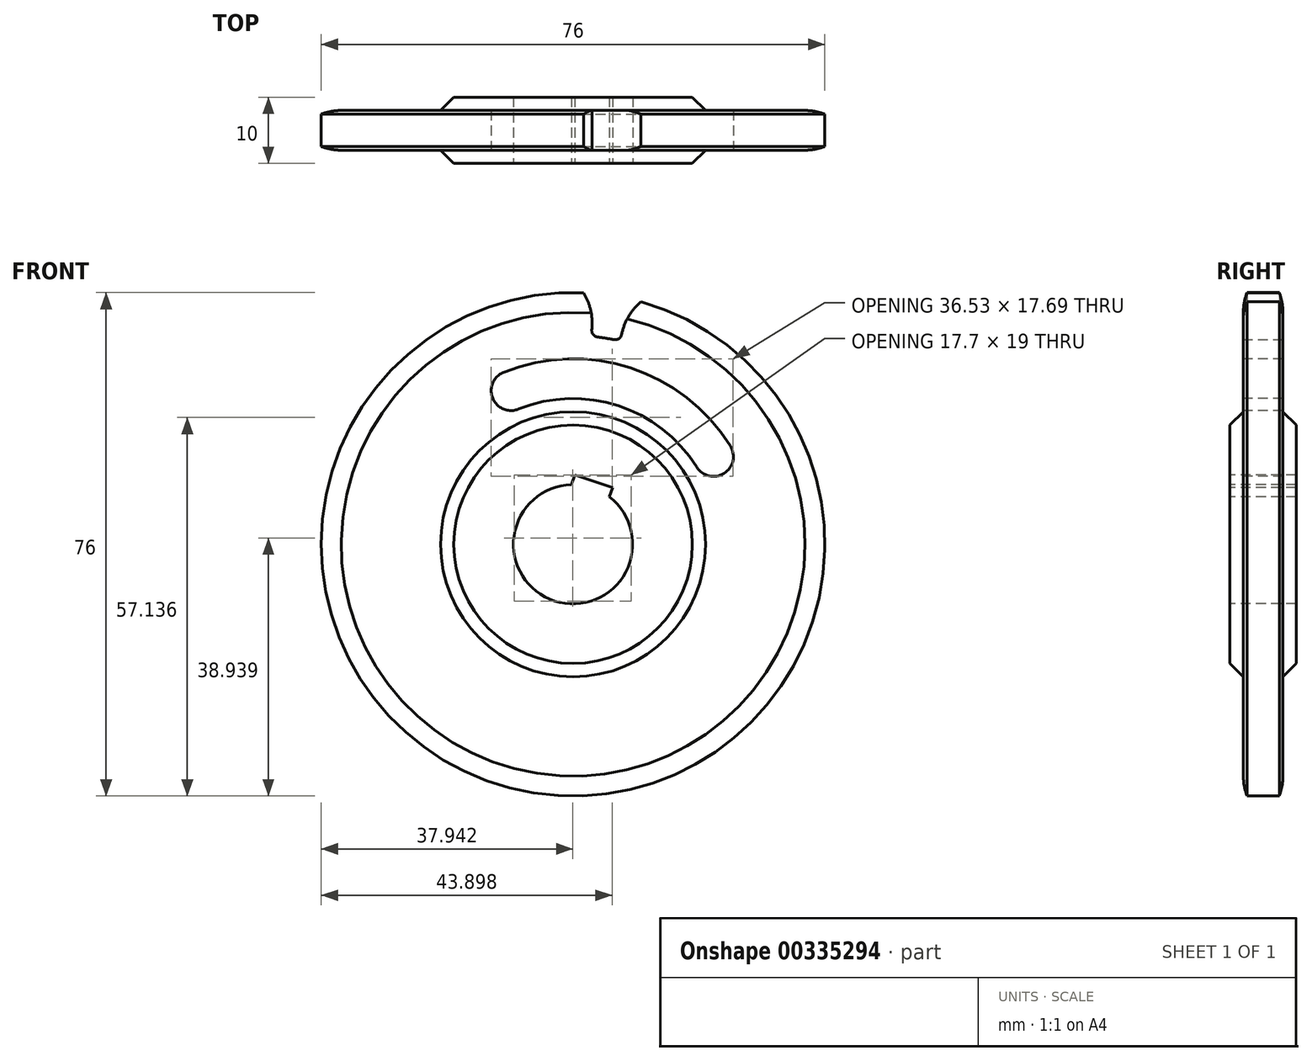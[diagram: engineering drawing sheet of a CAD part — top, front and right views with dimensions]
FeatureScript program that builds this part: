
annotation { "Feature Type Name" : "Feature", "Feature Type Description" : "" }
export const myFeature = defineFeature(function(context is Context, id is Id, definition is map)
    precondition{}
    {
        {
            var Q0;
            Q0=qCreatedBy(makeId("Front.planeOp"),FACE);
            var sketch = newSketch(context, id + "F0", { "sketchPlane" : qUnion([Q0])});
            skCircle(sketch, "E0", {"center": v(0, 0) * mm, "radius": 38 * mm});
            skSolve(sketch);
        }
        {
            var Q0;
            Q0=makeQuery(id+"F0.imprint","IMPRINT",FACE,{"disambiguationData":[TD([[makeQuery(id+"F0.imprint","IMPRINT",EDGE,{"derivedFrom":sQuery(id+"F0.wireOp",EDGE,"E0")}),1.0]])]});
            extrude(context, id + "F1", {"entities" : qUnion([Q0]), "depth" : 6 * mm, "symmetric" : true});
        }
        {
            var Q0;
            Q0=makeQuery(id+"F1.opExtrude","CAP_FACE",FACE,{"disambiguationData":[OSD([sQuery(id+"F0.wireOp",EDGE,"E0")])],"isStart":false});
            var sketch = newSketch(context, id + "F2", { "sketchPlane" : qUnion([Q0])});
            skLineSegment(sketch, "E1", {"start": v(0, 0) * mm, "end": v(0, 38) * mm, "construction": true});
            skArc(sketch, "E2", {"start": v(-1.57, 37.97) * mm, "mid": v(-0.79, 38) * mm, "end": v(0, 38) * mm, "construction": true});
            skCircle(sketch, "E3", {"center": v(0, 0) * mm, "radius": 35 * mm, "construction": true});
            skCircle(sketch, "E4", {"center": v(0, 0) * mm, "radius": 31.5 * mm, "construction": true});
            skArc(sketch, "E5", {"start": v(-1.58, 37.97) * mm, "mid": v(-2.67, 35.28) * mm, "end": v(-2.82, 32.39) * mm});
            skPoint(sketch, "E6", {"position": v(-2.75, 34.9) * mm});
            skLineSegment(sketch, "E7", {"start": v(0, 0) * mm, "end": v(-5.94, 37.53) * mm, "construction": true});
            skArc(sketch, "E8", {"start": v(-3.7, 31.28) * mm, "mid": v(-4.31, 31.2) * mm, "end": v(-4.93, 31.11) * mm});
            skPoint(sketch, "E9.visualSharp", {"position": v(-2.65, 31.39) * mm});
            skArc(sketch, "E9.filletArc", {"start": v(-3.7, 31.28) * mm, "mid": v(-3.03, 31.65) * mm, "end": v(-2.82, 32.39) * mm});
            skArc(sketch, "E10", {"start": v(-1.57, 37.97) * mm, "mid": v(-3.77, 37.81) * mm, "end": v(-5.94, 37.53) * mm});
            skArc(sketch, "E11.MirrorCS", {"start": v(-10.23, 36.6) * mm, "mid": v(-8.1, 37.13) * mm, "end": v(-5.94, 37.53) * mm});
            skArc(sketch, "E12.MirrorCS", {"start": v(-10.23, 36.6) * mm, "mid": v(-8.37, 34.38) * mm, "end": v(-7.32, 31.67) * mm});
            skArc(sketch, "E13.MirrorCS", {"start": v(-6.15, 30.9) * mm, "mid": v(-6.9, 31.04) * mm, "end": v(-7.32, 31.67) * mm});
            skArc(sketch, "E14.MirrorCS", {"start": v(-6.15, 30.9) * mm, "mid": v(-5.54, 31) * mm, "end": v(-4.93, 31.11) * mm});
            skSolve(sketch);
        }
        {
            var Q0;
            Q0 = qSketchRegion(id + "F2", true);
            extrude(context, id + "F3", {"entities" : qUnion([Q0]), "operationType" : NewBodyOperationType.REMOVE, "oppositeDirection" : true, "depth" : 25 * mm});
        }
        {
            var Q0;
            Q0=qCreatedBy(makeId("Front.planeOp"),FACE);
            var sketch = newSketch(context, id + "F4", { "sketchPlane" : qUnion([Q0])});
            skCircle(sketch, "E15", {"center": v(0, 0) * mm, "radius": 18 * mm});
            skSolve(sketch);
        }
        {
            var Q0;
            Q0 = qSketchRegion(id + "F4", true);
            extrude(context, id + "F5", {"entities" : qUnion([Q0]), "depth" : 10 * mm, "symmetric" : true});
        }
        {
            var Q0;
            Q0=makeQuery(id+"F1.opExtrude","SWEPT_BODY",BODY,{"disambiguationData":[OSD([sQuery(id+"F0.wireOp",EDGE,"E0")])]});
            var Q1;
            Q1=makeQuery(id+"F5.opExtrude","SWEPT_BODY",BODY,{"disambiguationData":[OSD([sQuery(id+"F4.wireOp",EDGE,"E15")])]});
            booleanBodies(context, id + "F6", {"operationType" : BooleanOperationType.UNION, "tools" : qUnion([Q0, Q1])});
        }
        {
            var Q0;
            Q0=makeQuery(id+"F6.opBoolean","INTERSECT",EDGE,{"derivedFrom":[makeQuery(id+"F1.opExtrude","CAP_FACE",FACE,{"disambiguationData":[OSD([sQuery(id+"F0.wireOp",EDGE,"E0")])],"isStart":true}),makeQuery(id+"F5.opExtrude","SWEPT_FACE",FACE,{"disambiguationData":[OSD([sQuery(id+"F4.wireOp",EDGE,"E15")])]})]});
            var Q1;
            Q1=makeQuery(id+"F6.opBoolean","INTERSECT",EDGE,{"derivedFrom":[makeQuery(id+"F1.opExtrude","CAP_FACE",FACE,{"disambiguationData":[OSD([sQuery(id+"F0.wireOp",EDGE,"E0")])],"isStart":false}),makeQuery(id+"F5.opExtrude","SWEPT_FACE",FACE,{"disambiguationData":[OSD([sQuery(id+"F4.wireOp",EDGE,"E15")])]})]});
            chamfer(context, id + "F7", {"entities" : qUnion([Q0, Q1]), "chamferType" : ChamferType.OFFSET_ANGLE, "width" : 2 * mm, "oppositeDirection" : false, "angle" : 45 * degree, "tangentPropagation" : true});
        }
        {
            var Q0;
            Q0=qCreatedBy(makeId("Right.planeOp"),FACE);
            var sketch = newSketch(context, id + "F8", { "sketchPlane" : qUnion([Q0])});
            skLineSegment(sketch, "E16", {"start": v(0, 0) * mm, "end": v(0, 51.39) * mm, "construction": true});
            skArc(sketch, "E17", {"start": v(-2.44, 38) * mm, "mid": v(-2.85, 36.52) * mm, "end": v(-3, 35) * mm});
            skArc(sketch, "E18", {"start": v(-2.44, 38) * mm, "mid": v(-4.7, 36.87) * mm, "end": v(-3, 35) * mm});
            skArc(sketch, "E19.MirrorCS", {"start": v(2.44, 38) * mm, "mid": v(4.7, 36.87) * mm, "end": v(3, 35) * mm});
            skArc(sketch, "E20.MirrorCS", {"start": v(2.44, 38) * mm, "mid": v(2.85, 36.52) * mm, "end": v(3, 35) * mm});
            skSolve(sketch);
        }
        {
            var Q0;
            Q0 = qSketchRegion(id + "F8", true);
            var Q1;
            {var subQ0=sQuery(id+"F4.wireOp",EDGE,"E15");Q1=makeQuery(id+"F7.opChamfer","BLEND_EDGE",EDGE,{"blendedFrom":[makeQuery(id+"F6.opBoolean","INTERSECT",EDGE,{"derivedFrom":[makeQuery(id+"F1.opExtrude","CAP_FACE",FACE,{"disambiguationData":[OSD([sQuery(id+"F0.wireOp",EDGE,"E0")])],"isStart":false}),makeQuery(id+"F5.opExtrude","SWEPT_FACE",FACE,{"disambiguationData":[OSD([subQ0])]})]}),makeQuery(id+"F5.opExtrude","CAP_FACE",FACE,{"disambiguationData":[OSD([subQ0])],"isStart":false})],"blendedInto":[makeQuery(id+"F5.opExtrude","CAP_FACE",FACE,{"disambiguationData":[OSD([subQ0])],"isStart":false})]});}
            revolve(context, id + "F9", {"operationType" : NewBodyOperationType.REMOVE, "entities" : qUnion([Q0]), "axis" : qUnion([Q1]), "revolveType" : RevolveType.FULL, "oppositeDirection" : true});
        }
        {
            var Q0;
            Q0=makeQuery(id+"F5.opExtrude","CAP_FACE",FACE,{"disambiguationData":[OSD([sQuery(id+"F4.wireOp",EDGE,"E15")])],"isStart":false});
            var sketch = newSketch(context, id + "F10", { "sketchPlane" : qUnion([Q0])});
            skCircle(sketch, "E21", {"center": v(0, 0) * mm, "radius": 9 * mm});
            skSolve(sketch);
        }
        {
            var Q0;
            Q0=makeQuery(id+"F10.imprint","IMPRINT",FACE,{"disambiguationData":[TD([[makeQuery(id+"F10.imprint","IMPRINT",EDGE,{"derivedFrom":sQuery(id+"F10.wireOp",EDGE,"E21")}),1.0]])]});
            extrude(context, id + "F11", {"entities" : qUnion([Q0]), "operationType" : NewBodyOperationType.REMOVE, "oppositeDirection" : true, "depth" : 25 * mm});
        }
        {
            var Q0;
            Q0=makeQuery(id+"F5.opExtrude","CAP_FACE",FACE,{"disambiguationData":[OSD([sQuery(id+"F4.wireOp",EDGE,"E15")])],"isStart":false});
            var sketch = newSketch(context, id + "F12", { "sketchPlane" : qUnion([Q0])});
            skLineSegment(sketch, "E22.bottom", {"start": v(3, 10) * mm, "end": v(-3, 10) * mm});
            skLineSegment(sketch, "E22.top", {"start": v(3, 5.66) * mm, "end": v(-3, 5.66) * mm});
            skLineSegment(sketch, "E22.left", {"start": v(3, 10) * mm, "end": v(3, 5.66) * mm});
            skLineSegment(sketch, "E22.right", {"start": v(-3, 10) * mm, "end": v(-3, 5.66) * mm});
            skPoint(sketch, "E22.middle", {"position": v(0, 7.83) * mm});
            skSolve(sketch);
        }
        {
            var Q0;
            {var subQ0=sQuery(id+"F12.wireOp",EDGE,"E22.bottom");Q0=makeQuery(id+"F12.imprint","IMPRINT",FACE,{"disambiguationData":[TD([[makeQuery(id+"F12.imprint","IMPRINT",EDGE,{"derivedFrom":subQ0}),1.0]])]});}
            extrude(context, id + "F13", {"entities" : qUnion([Q0]), "operationType" : NewBodyOperationType.REMOVE, "oppositeDirection" : true, "depth" : 25 * mm});
        }
        {
            var Q0;
            Q0=makeQuery(id+"F1.opExtrude","CAP_FACE",FACE,{"disambiguationData":[OSD([sQuery(id+"F0.wireOp",EDGE,"E0")])],"isStart":false});
            var sketch = newSketch(context, id + "F14", { "sketchPlane" : qUnion([Q0])});
            skLineSegment(sketch, "E23", {"start": v(0, 0) * mm, "end": v(-16.07, 19.15) * mm, "construction": true});
            skLineSegment(sketch, "E24", {"start": v(0, 0) * mm, "end": v(0, 26.53) * mm, "construction": true});
            skLineSegment(sketch, "E25", {"start": v(0, 0) * mm, "end": v(16.07, 19.15) * mm, "construction": true});
            skCircle(sketch, "E26", {"center": v(0, 0) * mm, "radius": 25 * mm, "construction": true});
            skArc(sketch, "E27", {"start": v(-18, 21.45) * mm, "mid": v(-18.37, 17.22) * mm, "end": v(-14.14, 16.85) * mm});
            skArc(sketch, "E28", {"start": v(13.66, 20.94) * mm, "mid": v(16.42, 16.17) * mm, "end": v(18, 21.45) * mm});
            skArc(sketch, "E29", {"start": v(-18, 21.45) * mm, "mid": v(0, 28) * mm, "end": v(18, 21.45) * mm});
            skArc(sketch, "E30", {"start": v(-14.14, 16.85) * mm, "mid": v(0, 22) * mm, "end": v(14.14, 16.85) * mm});
            skSolve(sketch);
        }
        {
            var Q0;
            Q0 = qSketchRegion(id + "F14", true);
            extrude(context, id + "F15", {"entities" : qUnion([Q0]), "operationType" : NewBodyOperationType.REMOVE, "oppositeDirection" : true, "depth" : 25 * mm});
        }
        {
            var Q0;
            Q0=makeQuery(id+"F1.opExtrude","SWEPT_BODY",BODY,{"disambiguationData":[OSD([sQuery(id+"F0.wireOp",EDGE,"E0")])]});
            var Q1;
            {var subQ0=sQuery(id+"F4.wireOp",EDGE,"E15");Q1=makeQuery(id+"F7.opChamfer","BLEND_EDGE",EDGE,{"blendedFrom":[makeQuery(id+"F6.opBoolean","INTERSECT",EDGE,{"derivedFrom":[makeQuery(id+"F1.opExtrude","CAP_FACE",FACE,{"disambiguationData":[OSD([sQuery(id+"F0.wireOp",EDGE,"E0")])],"isStart":false}),makeQuery(id+"F5.opExtrude","SWEPT_FACE",FACE,{"disambiguationData":[OSD([subQ0])]})]}),makeQuery(id+"F5.opExtrude","CAP_FACE",FACE,{"disambiguationData":[OSD([subQ0])],"isStart":false})],"blendedInto":[makeQuery(id+"F5.opExtrude","CAP_FACE",FACE,{"disambiguationData":[OSD([subQ0])],"isStart":false})]});}
            transform(context, id + "F16", {"entities" : qUnion([Q0]), "transformType" : TransformType.ROTATION, "transformAxis" : qUnion([Q1]), "angle" : 18 * degree, "oppositeDirection" : true, "makeCopy" : false});
        }
    });
